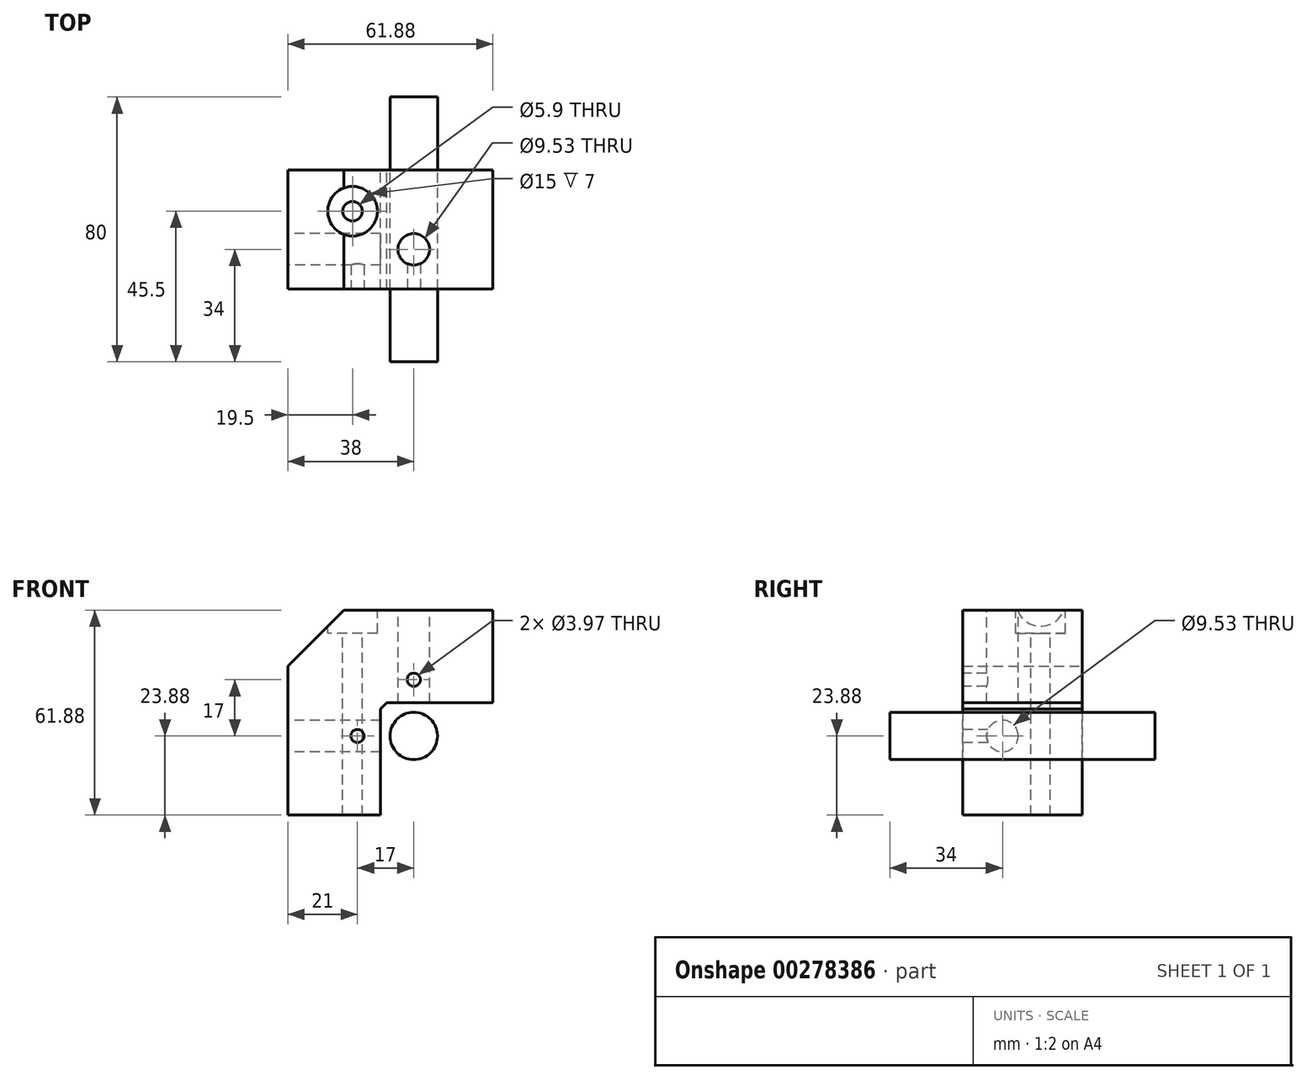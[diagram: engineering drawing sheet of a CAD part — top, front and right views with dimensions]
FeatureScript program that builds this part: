
annotation { "Feature Type Name" : "Feature", "Feature Type Description" : "" }
export const myFeature = defineFeature(function(context is Context, id is Id, definition is map)
    precondition{}
    {
        {
            var Q0;
            Q0=qCreatedBy(makeId("Front.planeOp"),FACE);
            var sketch = newSketch(context, id + "F0", { "sketchPlane" : qUnion([Q0])});
            skCircle(sketch, "E0", {"center": v(0, 0) * mm, "radius": 7.15 * mm});
            skLineSegment(sketch, "E1", {"start": v(-10, -23.88) * mm, "end": v(-10, 8.12) * mm});
            skLineSegment(sketch, "E2", {"start": v(-10, 8.12) * mm, "end": v(-8.12, 10) * mm});
            skLineSegment(sketch, "E3", {"start": v(-8.12, 10) * mm, "end": v(23.88, 10) * mm});
            skLineSegment(sketch, "E4", {"start": v(23.88, 10) * mm, "end": v(23.88, 38) * mm});
            skLineSegment(sketch, "E5", {"start": v(23.88, 38) * mm, "end": v(-21.12, 38) * mm});
            skLineSegment(sketch, "E6", {"start": v(-21.12, 38) * mm, "end": v(-38, 21.12) * mm});
            skLineSegment(sketch, "E7", {"start": v(-38, 21.12) * mm, "end": v(-38, -23.88) * mm});
            skLineSegment(sketch, "E8", {"start": v(-38, -23.88) * mm, "end": v(-10, -23.88) * mm});
            skLineSegment(sketch, "E9", {"start": v(-72.78, -23.88) * mm, "end": v(76.46, -23.88) * mm, "construction": true});
            skSolve(sketch);
        }
        {
            var Q0;
            Q0=makeQuery(id+"F0.imprint","IMPRINT",FACE,{"disambiguationData":[TD([[makeQuery(id+"F0.imprint","IMPRINT",EDGE,{"derivedFrom":sQuery(id+"F0.wireOp",EDGE,"E1")}),1.0]])]});
            extrude(context, id + "F1", {"entities" : qUnion([Q0]), "depth" : 18 * mm, "hasSecondDirection" : true, "secondDirectionOppositeDirection" : true, "secondDirectionDepth" : 18 * mm});
        }
        {
            var Q0;
            Q0=makeQuery(id+"F1.opExtrude","SWEPT_FACE",FACE,{"disambiguationData":[OSD([sQuery(id+"F0.wireOp",EDGE,"E7")])]});
            var sketch = newSketch(context, id + "F2", { "sketchPlane" : qUnion([Q0])});
            skCircle(sketch, "E10", {"center": v(6, 0) * mm, "radius": 4.76 * mm});
            skSolve(sketch);
        }
        {
            var Q0;
            Q0=makeQuery(id+"F2.imprint","IMPRINT",FACE,{"disambiguationData":[TD([[makeQuery(id+"F2.imprint","IMPRINT",EDGE,{"derivedFrom":sQuery(id+"F2.wireOp",EDGE,"E10")}),1.0]])]});
            extrude(context, id + "F3", {"entities" : qUnion([Q0]), "operationType" : NewBodyOperationType.REMOVE, "endBound" : BoundingType.UP_TO_NEXT, "oppositeDirection" : true, "depth" : 25 * mm});
        }
        {
            var Q0;
            Q0=makeQuery(id+"F0.imprint","IMPRINT",FACE,{"disambiguationData":[TD([[makeQuery(id+"F0.imprint","IMPRINT",EDGE,{"derivedFrom":sQuery(id+"F0.wireOp",EDGE,"E0")}),1.0]])]});
            extrude(context, id + "F4", {"entities" : qUnion([Q0]), "depth" : 40 * mm, "hasSecondDirection" : true, "secondDirectionOppositeDirection" : true, "secondDirectionDepth" : 40 * mm});
        }
        {
            var Q0;
            Q0=makeQuery(id+"F1.opExtrude","SWEPT_FACE",FACE,{"disambiguationData":[OSD([sQuery(id+"F0.wireOp",EDGE,"E5")])]});
            var sketch = newSketch(context, id + "F5", { "sketchPlane" : qUnion([Q0])});
            skCircle(sketch, "E11", {"center": v(0, -6) * mm, "radius": 4.76 * mm});
            skSolve(sketch);
        }
        {
            var Q0;
            Q0=makeQuery(id+"F5.imprint","IMPRINT",FACE,{"disambiguationData":[TD([[makeQuery(id+"F5.imprint","IMPRINT",EDGE,{"derivedFrom":sQuery(id+"F5.wireOp",EDGE,"E11")}),1.0]])]});
            extrude(context, id + "F6", {"entities" : qUnion([Q0]), "operationType" : NewBodyOperationType.REMOVE, "endBound" : BoundingType.UP_TO_NEXT, "oppositeDirection" : true, "depth" : 25 * mm});
        }
        {
            var Q0;
            Q0=makeQuery(id+"F1.opExtrude","SWEPT_FACE",FACE,{"disambiguationData":[OSD([sQuery(id+"F0.wireOp",EDGE,"E5")])]});
            var sketch = newSketch(context, id + "F7", { "sketchPlane" : qUnion([Q0])});
            skCircle(sketch, "E12", {"center": v(-18.5, 5.5) * mm, "radius": 7.5 * mm});
            skCircle(sketch, "E13", {"center": v(-18.5, 5.5) * mm, "radius": 2.95 * mm});
            skSolve(sketch);
        }
        {
            var Q0;
            Q0=makeQuery(id+"F1.opExtrude","CAP_FACE",FACE,{"disambiguationData":[OSD([sQuery(id+"F0.wireOp",EDGE,"E1"),sQuery(id+"F0.wireOp",EDGE,"E2"),sQuery(id+"F0.wireOp",EDGE,"E3"),sQuery(id+"F0.wireOp",EDGE,"E4"),sQuery(id+"F0.wireOp",EDGE,"E5"),sQuery(id+"F0.wireOp",EDGE,"E6"),sQuery(id+"F0.wireOp",EDGE,"E7"),sQuery(id+"F0.wireOp",EDGE,"E8")])],"isStart":false});
            var sketch = newSketch(context, id + "F8", { "sketchPlane" : qUnion([Q0])});
            skCircle(sketch, "E14", {"center": v(-17, 0) * mm, "radius": 1.98 * mm});
            skCircle(sketch, "E15", {"center": v(0, 17) * mm, "radius": 1.98 * mm});
            skSolve(sketch);
        }
        {
            var Q0;
            Q0=makeQuery(id+"F8.imprint","IMPRINT",FACE,{"disambiguationData":[TD([[makeQuery(id+"F8.imprint","IMPRINT",EDGE,{"derivedFrom":sQuery(id+"F8.wireOp",EDGE,"E14")}),1.0]])]});
            var Q1;
            Q1=makeQuery(id+"F8.imprint","IMPRINT",FACE,{"disambiguationData":[TD([[makeQuery(id+"F8.imprint","IMPRINT",EDGE,{"derivedFrom":sQuery(id+"F8.wireOp",EDGE,"E15")}),1.0]])]});
            extrude(context, id + "F9", {"entities" : qUnion([Q0, Q1]), "operationType" : NewBodyOperationType.REMOVE, "endBound" : BoundingType.UP_TO_NEXT, "oppositeDirection" : true, "depth" : 25 * mm});
        }
        {
            var Q0;
            Q0=makeQuery(id+"F7.imprint","IMPRINT",FACE,{"disambiguationData":[TD([[makeQuery(id+"F7.imprint","IMPRINT",EDGE,{"derivedFrom":sQuery(id+"F7.wireOp",EDGE,"E13")}),1.0]])]});
            extrude(context, id + "F10", {"entities" : qUnion([Q0]), "operationType" : NewBodyOperationType.REMOVE, "endBound" : BoundingType.THROUGH_ALL, "oppositeDirection" : true, "depth" : 25 * mm});
        }
        {
            var Q0;
            {var subQ0=sQuery(id+"F7.wireOp",EDGE,"E12");var subQ1=makeQuery(id+"F1.opExtrude","SWEPT_EDGE",EDGE,{"disambiguationData":[OSD([sQuery(id+"F0.wireOp",EDGE,"E5"),sQuery(id+"F0.wireOp",EDGE,"E6")])]});var subQ2=makeQuery(id+"F7.imprint","INTERSECT",VERTEX,{"disambiguationData":[OD(0.0)],"derivedFrom":[subQ1,subQ0]});Q0=makeQuery(id+"F7.imprint","IMPRINT",FACE,{"disambiguationData":[TD([[makeQuery(id+"F7.imprint","IMPRINT",EDGE,{"disambiguationData":[TD([[subQ2,-1.0]])],"derivedFrom":subQ0}),1.0]])]});}
            var Q1;
            Q1=makeQuery(id+"F7.imprint","IMPRINT",FACE,{"disambiguationData":[TD([[makeQuery(id+"F7.imprint","IMPRINT",EDGE,{"derivedFrom":sQuery(id+"F7.wireOp",EDGE,"E13")}),-1.0]])]});
            extrude(context, id + "F11", {"entities" : qUnion([Q0, Q1]), "operationType" : NewBodyOperationType.REMOVE, "oppositeDirection" : true, "depth" : 7 * mm});
        }
    });
